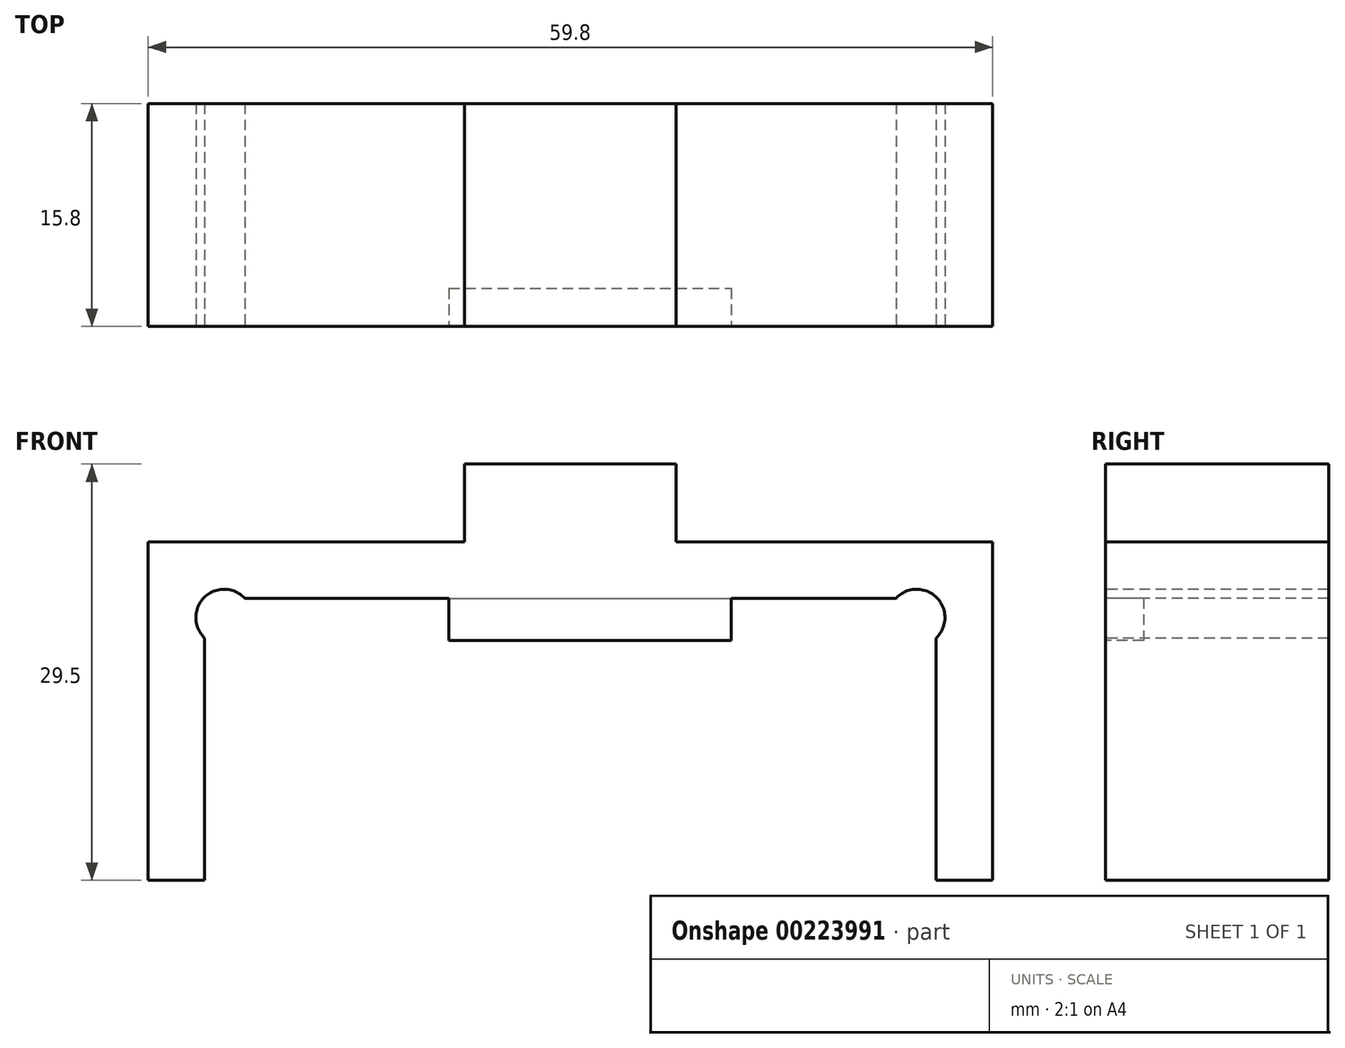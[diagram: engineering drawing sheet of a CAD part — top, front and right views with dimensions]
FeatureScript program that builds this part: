
annotation { "Feature Type Name" : "Feature", "Feature Type Description" : "" }
export const myFeature = defineFeature(function(context is Context, id is Id, definition is map)
    precondition{}
    {
        {
            var Q0;
            Q0=qCreatedBy(makeId("Front.planeOp"),FACE);
            var sketch = newSketch(context, id + "F0", { "sketchPlane" : qUnion([Q0])});
            skLineSegment(sketch, "E0", {"start": v(-25.9, 0) * mm, "end": v(25.9, 0) * mm});
            skLineSegment(sketch, "E1", {"start": v(25.9, 0) * mm, "end": v(25.9, -20) * mm});
            skLineSegment(sketch, "E2", {"start": v(25.9, -20) * mm, "end": v(29.9, -20) * mm});
            skLineSegment(sketch, "E3", {"start": v(29.9, -20) * mm, "end": v(29.9, 4) * mm});
            skLineSegment(sketch, "E4", {"start": v(29.9, 4) * mm, "end": v(-29.9, 4) * mm});
            skLineSegment(sketch, "E5", {"start": v(-29.9, 4) * mm, "end": v(-29.9, -20) * mm});
            skLineSegment(sketch, "E6", {"start": v(-25.9, 0) * mm, "end": v(-25.9, -20) * mm});
            skLineSegment(sketch, "E7", {"start": v(-29.9, -20) * mm, "end": v(-25.9, -20) * mm});
            skLineSegment(sketch, "E8", {"start": v(0, 4) * mm, "end": v(0, 0) * mm, "construction": true});
            skSolve(sketch);
        }
        {
            var Q0;
            Q0 = qSketchRegion(id + "F0", true);
            extrude(context, id + "F1", {"entities" : qUnion([Q0]), "depth" : 15.8 * mm});
        }
        {
            var Q0;
            Q0=makeQuery(id+"F9LglXzXjf0wFS4_1.boolean.opBoolean","MERGE",FACE,{"derivedFrom":[makeQuery(id+"F1.opExtrude","CAP_FACE",FACE,{"disambiguationData":[OSD([sQuery(id+"F0.wireOp",EDGE,"E0"),sQuery(id+"F0.wireOp",EDGE,"E1"),sQuery(id+"F0.wireOp",EDGE,"E2"),sQuery(id+"F0.wireOp",EDGE,"E3"),sQuery(id+"F0.wireOp",EDGE,"E4"),sQuery(id+"F0.wireOp",EDGE,"E5"),sQuery(id+"F0.wireOp",EDGE,"E6"),sQuery(id+"F0.wireOp",EDGE,"E7")])],"isStart":false}),makeQuery(id+"F9LglXzXjf0wFS4_1.opExtrude","SWEPT_FACE",FACE,{"disambiguationData":[OSD([sQuery(id+"FYARErsVbTCtNrI_1.wireOp",EDGE,"GXMndrnz-ynjM-LKyG-2qyd-MET51fliCLm4.top")])]}),makeQuery(id+"F9LglXzXjf0wFS4_1.opExtrude","SWEPT_FACE",FACE,{"disambiguationData":[OSD([sQuery(id+"FYARErsVbTCtNrI_1.wireOp",EDGE,"EI0ukCVB-susb-Reoy-ppd6-CUHXXt3CTDaQ.top")])]})]});
            var sketch = newSketch(context, id + "F2", { "sketchPlane" : qUnion([Q0])});
            skLineSegment(sketch, "E9.bottom", {"start": v(11.4, 0) * mm, "end": v(-8.6, 0) * mm});
            skLineSegment(sketch, "E9.top", {"start": v(11.4, -3) * mm, "end": v(-8.6, -3) * mm});
            skLineSegment(sketch, "E9.left", {"start": v(11.4, 0) * mm, "end": v(11.4, -3) * mm});
            skLineSegment(sketch, "E9.right", {"start": v(-8.6, 0) * mm, "end": v(-8.6, -3) * mm});
            skSolve(sketch);
        }
        {
            var Q0;
            Q0 = qSketchRegion(id + "F2", true);
            extrude(context, id + "F3", {"entities" : qUnion([Q0]), "operationType" : NewBodyOperationType.ADD, "oppositeDirection" : true, "depth" : 2.7 * mm});
        }
        {
            var Q0;
            Q0=makeQuery(id+"F1.opExtrude","SWEPT_FACE",FACE,{"disambiguationData":[OSD([sQuery(id+"F0.wireOp",EDGE,"E4")])]});
            var sketch = newSketch(context, id + "F4", { "sketchPlane" : qUnion([Q0])});
            skLineSegment(sketch, "E10", {"start": v(0, 0) * mm, "end": v(0, -15.8) * mm, "construction": true});
            skLineSegment(sketch, "E11.bottom", {"start": v(7.5, 0) * mm, "end": v(-7.5, 0) * mm});
            skLineSegment(sketch, "E11.top", {"start": v(7.5, -15.8) * mm, "end": v(-7.5, -15.8) * mm});
            skLineSegment(sketch, "E11.left", {"start": v(7.5, 0) * mm, "end": v(7.5, -15.8) * mm});
            skLineSegment(sketch, "E11.right", {"start": v(-7.5, 0) * mm, "end": v(-7.5, -15.8) * mm});
            skPoint(sketch, "E11.middle", {"position": v(0, -7.9) * mm});
            skSolve(sketch);
        }
        {
            var Q0;
            Q0 = qSketchRegion(id + "F4", true);
            extrude(context, id + "F5", {"entities" : qUnion([Q0]), "operationType" : NewBodyOperationType.ADD, "depth" : 5.5 * mm});
        }
        {
            var Q0;
            Q0=makeQuery(id+"F5.boolean.opBoolean","MERGE",FACE,{"derivedFrom":[makeQuery(id+"F3.boolean.opBoolean","MERGE",FACE,{"derivedFrom":[makeQuery(id+"F1.opExtrude","CAP_FACE",FACE,{"disambiguationData":[OSD([sQuery(id+"F0.wireOp",EDGE,"E0"),sQuery(id+"F0.wireOp",EDGE,"E1"),sQuery(id+"F0.wireOp",EDGE,"E2"),sQuery(id+"F0.wireOp",EDGE,"E3"),sQuery(id+"F0.wireOp",EDGE,"E4"),sQuery(id+"F0.wireOp",EDGE,"E5"),sQuery(id+"F0.wireOp",EDGE,"E6"),sQuery(id+"F0.wireOp",EDGE,"E7")])],"isStart":false}),makeQuery(id+"F3.opExtrude","CAP_FACE",FACE,{"disambiguationData":[OSD([sQuery(id+"F2.wireOp",EDGE,"E9.bottom"),sQuery(id+"F2.wireOp",EDGE,"E9.top"),sQuery(id+"F2.wireOp",EDGE,"E9.left"),sQuery(id+"F2.wireOp",EDGE,"E9.right")])],"isStart":true})]}),makeQuery(id+"F5.opExtrude","SWEPT_FACE",FACE,{"disambiguationData":[OSD([sQuery(id+"F4.wireOp",EDGE,"E11.top")])]})]});
            var sketch = newSketch(context, id + "F6", { "sketchPlane" : qUnion([Q0])});
            skLineSegment(sketch, "E12", {"start": v(-25.9, 0) * mm, "end": v(-7.12, -18.78) * mm, "construction": true});
            skCircle(sketch, "E13", {"center": v(-24.53, -1.37) * mm, "radius": 2 * mm});
            skCircle(sketch, "E14.MirrorC", {"center": v(24.53, -1.37) * mm, "radius": 2 * mm});
            skSolve(sketch);
        }
        {
            var Q0;
            Q0 = qSketchRegion(id + "F6", true);
            extrude(context, id + "F7", {"entities" : qUnion([Q0]), "operationType" : NewBodyOperationType.REMOVE, "endBound" : BoundingType.THROUGH_ALL, "oppositeDirection" : true, "depth" : 25 * mm});
        }
    });
